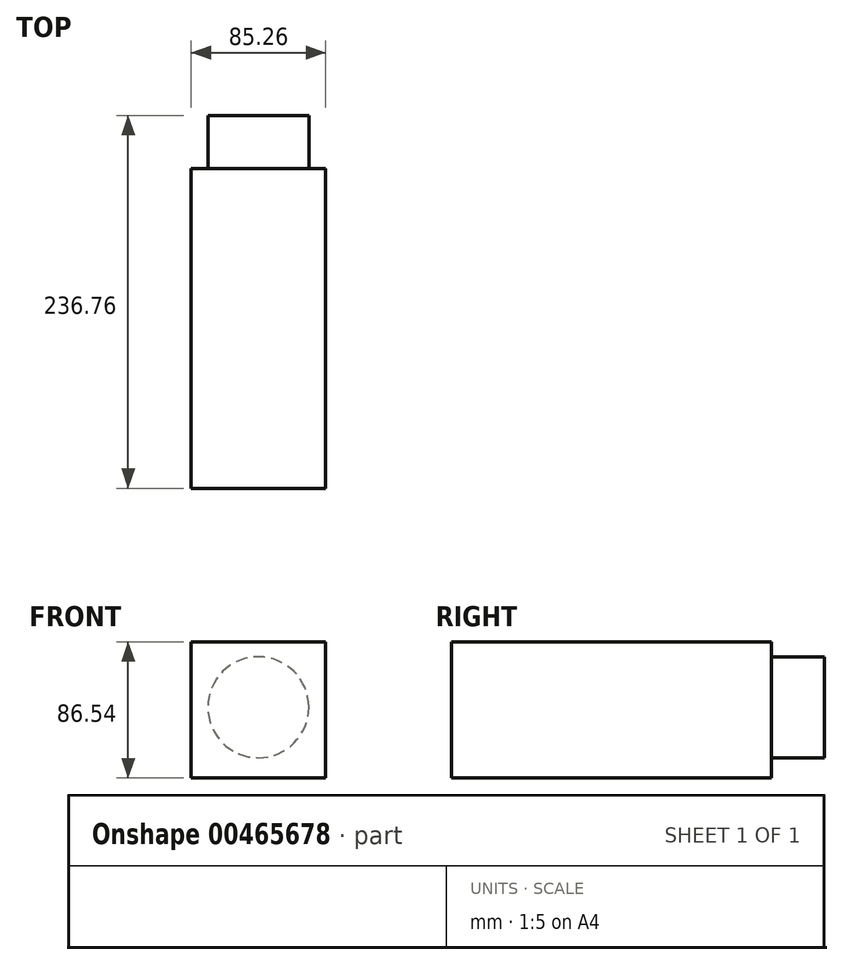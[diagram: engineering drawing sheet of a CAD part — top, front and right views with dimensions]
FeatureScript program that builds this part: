
annotation { "Feature Type Name" : "Feature", "Feature Type Description" : "" }
export const myFeature = defineFeature(function(context is Context, id is Id, definition is map)
    precondition{}
    {
        {
            var Q0;
            Q0=qCreatedBy(makeId("Front.planeOp"),FACE);
            var sketch = newSketch(context, id + "F0", { "sketchPlane" : qUnion([Q0])});
            skLineSegment(sketch, "E0.bottom", {"start": v(0, 0) * mm, "end": v(85.26, 0) * mm});
            skLineSegment(sketch, "E0.top", {"start": v(0, 86.54) * mm, "end": v(85.26, 86.54) * mm});
            skLineSegment(sketch, "E0.left", {"start": v(0, 0) * mm, "end": v(0, 86.54) * mm});
            skLineSegment(sketch, "E0.right", {"start": v(85.26, 0) * mm, "end": v(85.26, 86.54) * mm});
            skSolve(sketch);
        }
        {
            var Q0;
            Q0=makeQuery(id+"F0.imprint","IMPRINT",FACE,{"disambiguationData":[TD([[makeQuery(id+"F0.imprint","IMPRINT",EDGE,{"derivedFrom":sQuery(id+"F0.wireOp",EDGE,"E0.bottom")}),1.0]])]});
            extrude(context, id + "F1", {"entities" : qUnion([Q0]), "depth" : 203.2 * mm});
        }
        {
            var Q0;
            Q0=makeQuery(id+"F1.opExtrude","CAP_FACE",FACE,{"disambiguationData":[OSD([sQuery(id+"F0.wireOp",EDGE,"E0.bottom"),sQuery(id+"F0.wireOp",EDGE,"E0.top"),sQuery(id+"F0.wireOp",EDGE,"E0.left"),sQuery(id+"F0.wireOp",EDGE,"E0.right")])],"isStart":false});
            var sketch = newSketch(context, id + "F2", { "sketchPlane" : qUnion([Q0])});
            skCircle(sketch, "E1", {"center": v(42.63, 44.93) * mm, "radius": 32.03 * mm});
            skPoint(sketch, "E1.centerSnap0", {"position": v(42.63, 86.54) * mm});
            skSolve(sketch);
        }
        {
            var Q0;
            Q0=makeQuery(id+"F2.imprint","IMPRINT",FACE,{"disambiguationData":[TD([[makeQuery(id+"F2.imprint","IMPRINT",EDGE,{"derivedFrom":sQuery(id+"F2.wireOp",EDGE,"E1")}),1.0]])]});
            extrude(context, id + "F3", {"entities" : qUnion([Q0]), "operationType" : NewBodyOperationType.ADD, "endBound" : BoundingType.THROUGH_ALL, "oppositeDirection" : true, "depth" : 25.4 * mm});
        }
    });
